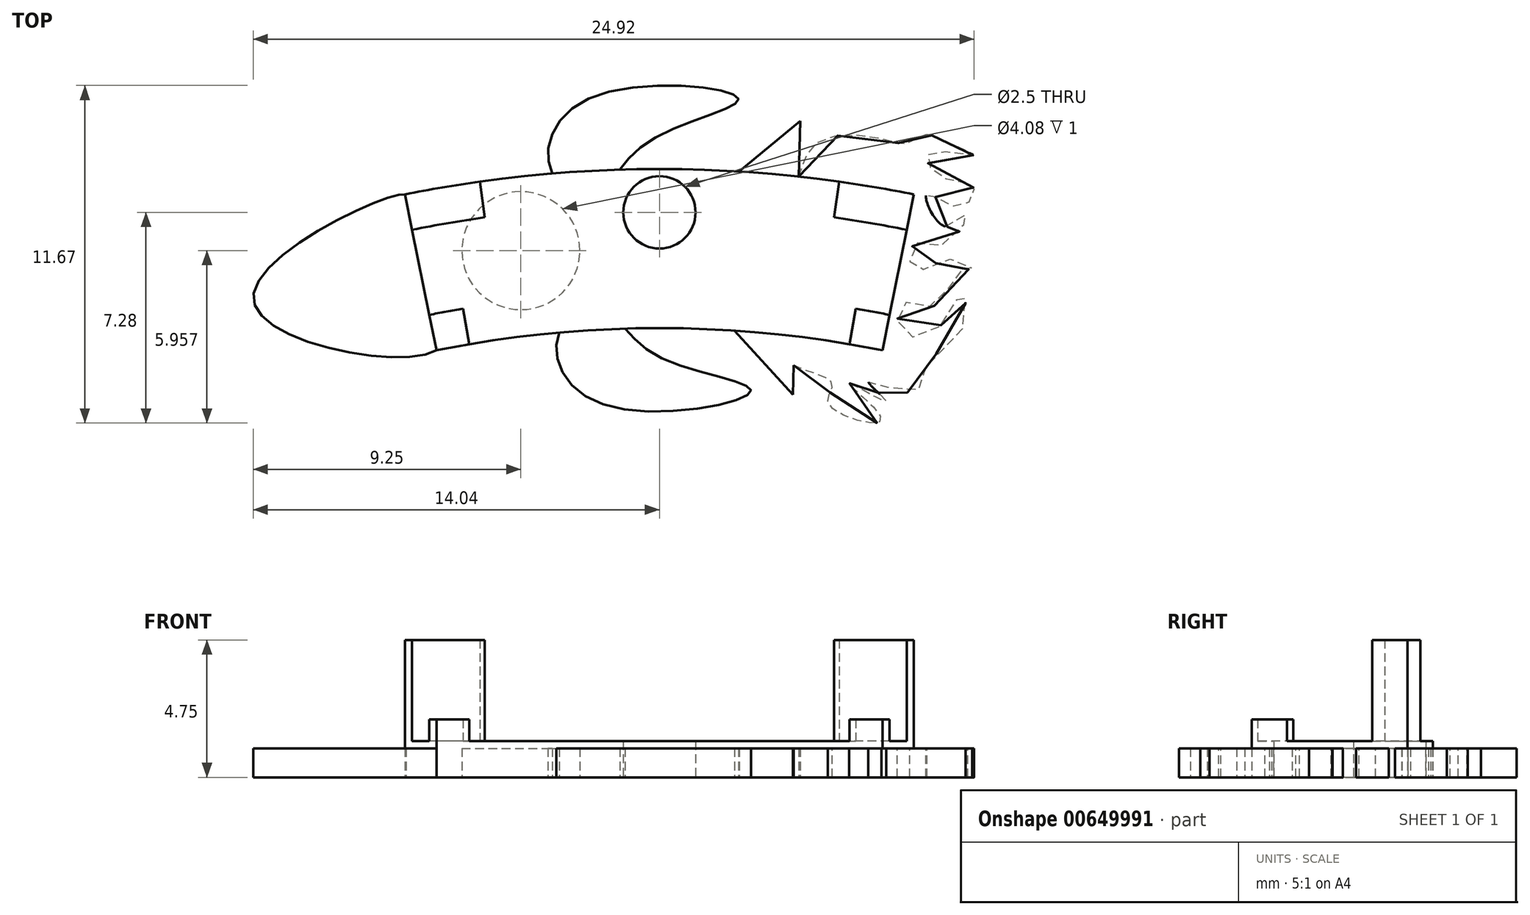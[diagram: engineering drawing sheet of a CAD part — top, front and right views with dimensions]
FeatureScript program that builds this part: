
annotation { "Feature Type Name" : "Feature", "Feature Type Description" : "" }
export const myFeature = defineFeature(function(context is Context, id is Id, definition is map)
    precondition{}
    {
        {
            var Q0;
            Q0=qCreatedBy(makeId("Top.planeOp"),FACE);
            var sketch = newSketch(context, id + "F0", { "sketchPlane" : qUnion([Q0])});
            skCircle(sketch, "E0", {"center": v(0, 0) * mm, "radius": 39 * mm});
            skCircle(sketch, "E1", {"center": v(0, 0) * mm, "radius": 44.5 * mm});
            skCircle(sketch, "E2", {"center": v(0, 43) * mm, "radius": 1.25 * mm});
            skCircle(sketch, "E3", {"center": v(0, 43) * mm, "radius": 6 * mm});
            skLineSegment(sketch, "E4", {"start": v(-7.7, 38.23) * mm, "end": v(-8.8, 43.62) * mm});
            skLineSegment(sketch, "E5", {"start": v(7.7, 38.23) * mm, "end": v(8.8, 43.62) * mm});
            skLineSegment(sketch, "E6", {"start": v(-7.5, 43.86) * mm, "end": v(-6.58, 38.44) * mm});
            skLineSegment(sketch, "E7", {"start": v(6.58, 38.44) * mm, "end": v(7.5, 43.86) * mm});
            skCircle(sketch, "E8", {"center": v(0, 0) * mm, "radius": 40.25 * mm});
            skCircle(sketch, "E9", {"center": v(0, 0) * mm, "radius": 43.25 * mm});
            skSolve(sketch);
        }
        {
            var Q0;
            {var subQ0=sQuery(id+"F0.wireOp",EDGE,"E7");var subQ1=sQuery(id+"F0.wireOp",EDGE,"E1");var subQ2=makeQuery(id+"F0.imprint","INTERSECT",VERTEX,{"derivedFrom":[subQ1,subQ0]});Q0=makeQuery(id+"F0.imprint","IMPRINT",FACE,{"disambiguationData":[TD([[makeQuery(id+"F0.imprint","IMPRINT",EDGE,{"disambiguationData":[TD([[subQ2,-1.0]])],"derivedFrom":subQ1}),1.0]])]});}
            var Q1;
            {var subQ0=sQuery(id+"F0.wireOp",EDGE,"E6");var subQ1=sQuery(id+"F0.wireOp",EDGE,"E1");var subQ2=makeQuery(id+"F0.imprint","INTERSECT",VERTEX,{"derivedFrom":[subQ1,subQ0]});Q1=makeQuery(id+"F0.imprint","IMPRINT",FACE,{"disambiguationData":[TD([[makeQuery(id+"F0.imprint","IMPRINT",EDGE,{"disambiguationData":[TD([[subQ2,1.0]])],"derivedFrom":subQ1}),1.0]])]});}
            var Q2;
            {var subQ0=sQuery(id+"F0.wireOp",EDGE,"E3");var subQ1=sQuery(id+"F0.wireOp",EDGE,"E1");var subQ2=makeQuery(id+"F0.imprint","INTERSECT",VERTEX,{"disambiguationData":[OD(0.0)],"derivedFrom":[subQ1,subQ0]});Q2=makeQuery(id+"F0.imprint","IMPRINT",FACE,{"disambiguationData":[TD([[makeQuery(id+"F0.imprint","IMPRINT",EDGE,{"disambiguationData":[TD([[subQ2,-1.0]])],"derivedFrom":subQ1}),1.0]])]});}
            var Q3;
            {var subQ0=sQuery(id+"F0.wireOp",EDGE,"E8");var subQ1=sQuery(id+"F0.wireOp",EDGE,"E3");var subQ2=makeQuery(id+"F0.imprint","INTERSECT",VERTEX,{"disambiguationData":[OD(1.0)],"derivedFrom":[subQ1,subQ0]});Q3=makeQuery(id+"F0.imprint","IMPRINT",FACE,{"disambiguationData":[TD([[makeQuery(id+"F0.imprint","IMPRINT",EDGE,{"disambiguationData":[TD([[subQ2,-1.0]])],"derivedFrom":subQ1}),-1.0]])]});}
            var Q4;
            {var subQ3=sQuery(id+"F0.wireOp",EDGE,"E9");var subQ5=sQuery(id+"F0.wireOp",EDGE,"E2");var subQ6=makeQuery(id+"F0.imprint","INTERSECT",VERTEX,{"disambiguationData":[OD(0.0)],"derivedFrom":[subQ5,subQ3]});Q4=makeQuery(id+"F0.imprint","IMPRINT",FACE,{"disambiguationData":[TD([[makeQuery(id+"F0.imprint","IMPRINT",EDGE,{"disambiguationData":[TD([[subQ6,1.0]])],"derivedFrom":subQ5}),-1.0]])]});}
            var Q5;
            {var subQ0=sQuery(id+"F0.wireOp",EDGE,"E9");var subQ1=sQuery(id+"F0.wireOp",EDGE,"E3");var subQ2=makeQuery(id+"F0.imprint","INTERSECT",VERTEX,{"disambiguationData":[OD(0.0)],"derivedFrom":[subQ1,subQ0]});Q5=makeQuery(id+"F0.imprint","IMPRINT",FACE,{"disambiguationData":[TD([[makeQuery(id+"F0.imprint","IMPRINT",EDGE,{"disambiguationData":[TD([[subQ2,-1.0]])],"derivedFrom":subQ1}),-1.0]])]});}
            var Q6;
            {var subQ0=sQuery(id+"F0.wireOp",EDGE,"E6");var subQ1=sQuery(id+"F0.wireOp",EDGE,"E0");var subQ2=makeQuery(id+"F0.imprint","INTERSECT",VERTEX,{"derivedFrom":[subQ1,subQ0]});Q6=makeQuery(id+"F0.imprint","IMPRINT",FACE,{"disambiguationData":[TD([[makeQuery(id+"F0.imprint","IMPRINT",EDGE,{"disambiguationData":[TD([[subQ2,1.0]])],"derivedFrom":subQ1}),-1.0]])]});}
            var Q7;
            {var subQ0=sQuery(id+"F0.wireOp",EDGE,"E3");var subQ1=sQuery(id+"F0.wireOp",EDGE,"E0");var subQ2=makeQuery(id+"F0.imprint","INTERSECT",VERTEX,{"disambiguationData":[OD(0.0)],"derivedFrom":[subQ1,subQ0]});Q7=makeQuery(id+"F0.imprint","IMPRINT",FACE,{"disambiguationData":[TD([[makeQuery(id+"F0.imprint","IMPRINT",EDGE,{"disambiguationData":[TD([[subQ2,-1.0]])],"derivedFrom":subQ1}),-1.0]])]});}
            var Q8;
            {var subQ0=sQuery(id+"F0.wireOp",EDGE,"E7");var subQ1=sQuery(id+"F0.wireOp",EDGE,"E0");var subQ2=makeQuery(id+"F0.imprint","INTERSECT",VERTEX,{"derivedFrom":[subQ1,subQ0]});Q8=makeQuery(id+"F0.imprint","IMPRINT",FACE,{"disambiguationData":[TD([[makeQuery(id+"F0.imprint","IMPRINT",EDGE,{"disambiguationData":[TD([[subQ2,-1.0]])],"derivedFrom":subQ1}),-1.0]])]});}
            var Q9;
            {var subQ0=sQuery(id+"F0.wireOp",EDGE,"E8");var subQ1=sQuery(id+"F0.wireOp",EDGE,"E5");var subQ2=makeQuery(id+"F0.imprint","INTERSECT",VERTEX,{"derivedFrom":[subQ1,subQ0]});Q9=makeQuery(id+"F0.imprint","IMPRINT",FACE,{"disambiguationData":[TD([[makeQuery(id+"F0.imprint","IMPRINT",EDGE,{"disambiguationData":[TD([[subQ2,-1.0]])],"derivedFrom":subQ1}),1.0]])]});}
            var Q10;
            {var subQ0=sQuery(id+"F0.wireOp",EDGE,"E8");var subQ1=sQuery(id+"F0.wireOp",EDGE,"E4");var subQ2=makeQuery(id+"F0.imprint","INTERSECT",VERTEX,{"derivedFrom":[subQ1,subQ0]});Q10=makeQuery(id+"F0.imprint","IMPRINT",FACE,{"disambiguationData":[TD([[makeQuery(id+"F0.imprint","IMPRINT",EDGE,{"disambiguationData":[TD([[subQ2,-1.0]])],"derivedFrom":subQ1}),-1.0]])]});}
            extrude(context, id + "F1", {"entities" : qUnion([Q0, Q1, Q2, Q3, Q4, Q5, Q6, Q7, Q8, Q9, Q10]), "depth" : 1.25 * mm, "offsetDistance" : 25 * mm});
        }
        {
            var Q0;
            Q0=qCreatedBy(makeId("Top.planeOp"),FACE);
            var sketch = newSketch(context, id + "F2", { "sketchPlane" : qUnion([Q0])});
            skCircle(sketch, "E10", {"center": v(0, 0) * mm, "radius": 39 * mm});
            skCircle(sketch, "E11", {"center": v(0, 0) * mm, "radius": 44.5 * mm});
            skCircle(sketch, "E12", {"center": v(0, 43) * mm, "radius": 0.85 * mm});
            skCircle(sketch, "E13", {"center": v(0, 43) * mm, "radius": 6 * mm});
            skLineSegment(sketch, "E14", {"start": v(-7.7, 38.23) * mm, "end": v(-8.8, 43.62) * mm});
            skLineSegment(sketch, "E15", {"start": v(7.7, 38.23) * mm, "end": v(8.8, 43.62) * mm});
            skLineSegment(sketch, "E16", {"start": v(-6.2, 44.06) * mm, "end": v(-5.44, 38.62) * mm});
            skLineSegment(sketch, "E17", {"start": v(5.44, 38.62) * mm, "end": v(6.2, 44.06) * mm});
            skCircle(sketch, "E18", {"center": v(0, 0) * mm, "radius": 40.25 * mm});
            skCircle(sketch, "E19", {"center": v(0, 0) * mm, "radius": 43.25 * mm});
            skSolve(sketch);
        }
        {
            var Q0;
            {var subQ0=sQuery(id+"F2.wireOp",EDGE,"E15");var subQ1=sQuery(id+"F2.wireOp",EDGE,"E11");var subQ2=makeQuery(id+"F2.imprint","INTERSECT",VERTEX,{"derivedFrom":[subQ1,subQ0]});Q0=makeQuery(id+"F2.imprint","IMPRINT",FACE,{"disambiguationData":[TD([[makeQuery(id+"F2.imprint","IMPRINT",EDGE,{"disambiguationData":[TD([[subQ2,-1.0]])],"derivedFrom":subQ1}),1.0]])]});}
            var Q1;
            {var subQ0=sQuery(id+"F2.wireOp",EDGE,"E14");var subQ1=sQuery(id+"F2.wireOp",EDGE,"E11");var subQ2=makeQuery(id+"F2.imprint","INTERSECT",VERTEX,{"derivedFrom":[subQ1,subQ0]});Q1=makeQuery(id+"F2.imprint","IMPRINT",FACE,{"disambiguationData":[TD([[makeQuery(id+"F2.imprint","IMPRINT",EDGE,{"disambiguationData":[TD([[subQ2,1.0]])],"derivedFrom":subQ1}),1.0]])]});}
            extrude(context, id + "F3", {"entities" : qUnion([Q0, Q1]), "operationType" : NewBodyOperationType.ADD, "depth" : 4.75 * mm, "offsetDistance" : 25 * mm});
        }
        {
            var Q0;
            Q0=qCreatedBy(makeId("Top.planeOp"),FACE);
            var sketch = newSketch(context, id + "F4", { "sketchPlane" : qUnion([Q0])});
            skCircle(sketch, "E20", {"center": v(0, 0) * mm, "radius": 39 * mm});
            skCircle(sketch, "E21", {"center": v(0, 0) * mm, "radius": 44.5 * mm});
            skCircle(sketch, "E22", {"center": v(0, 43) * mm, "radius": 0.85 * mm});
            skCircle(sketch, "E23", {"center": v(0, 43) * mm, "radius": 6 * mm});
            skLineSegment(sketch, "E24", {"start": v(-7.7, 38.23) * mm, "end": v(-8.8, 43.62) * mm});
            skLineSegment(sketch, "E25", {"start": v(7.7, 38.23) * mm, "end": v(8.8, 43.62) * mm});
            skLineSegment(sketch, "E26", {"start": v(-7.5, 43.86) * mm, "end": v(-6.58, 38.44) * mm});
            skLineSegment(sketch, "E27", {"start": v(6.58, 38.44) * mm, "end": v(7.5, 43.86) * mm});
            skCircle(sketch, "E28", {"center": v(0, 0) * mm, "radius": 40.25 * mm});
            skCircle(sketch, "E29", {"center": v(0, 0) * mm, "radius": 43.25 * mm});
            skSolve(sketch);
        }
        {
            var Q0;
            {var subQ0=sQuery(id+"F4.wireOp",EDGE,"E24");var subQ1=sQuery(id+"F4.wireOp",EDGE,"E20");var subQ2=makeQuery(id+"F4.imprint","INTERSECT",VERTEX,{"derivedFrom":[subQ1,subQ0]});Q0=makeQuery(id+"F4.imprint","IMPRINT",FACE,{"disambiguationData":[TD([[makeQuery(id+"F4.imprint","IMPRINT",EDGE,{"disambiguationData":[TD([[subQ2,1.0]])],"derivedFrom":subQ1}),-1.0]])]});}
            var Q1;
            {var subQ0=sQuery(id+"F4.wireOp",EDGE,"E25");var subQ1=sQuery(id+"F4.wireOp",EDGE,"E20");var subQ2=makeQuery(id+"F4.imprint","INTERSECT",VERTEX,{"derivedFrom":[subQ1,subQ0]});Q1=makeQuery(id+"F4.imprint","IMPRINT",FACE,{"disambiguationData":[TD([[makeQuery(id+"F4.imprint","IMPRINT",EDGE,{"disambiguationData":[TD([[subQ2,-1.0]])],"derivedFrom":subQ1}),-1.0]])]});}
            extrude(context, id + "F5", {"entities" : qUnion([Q0, Q1]), "operationType" : NewBodyOperationType.ADD, "depth" : 2 * mm, "offsetDistance" : 25 * mm});
        }
        {
            var Q0;
            {var subQ0=sQuery(id+"F4.wireOp",EDGE,"E28");var subQ1=sQuery(id+"F4.wireOp",EDGE,"E20");var subQ2=sQuery(id+"F2.wireOp",EDGE,"E19");var subQ3=sQuery(id+"F2.wireOp",EDGE,"E11");Q0=makeQuery(id+"F5.boolean.opBoolean","MERGE",FACE,{"derivedFrom":[makeQuery(id+"F3.boolean.opBoolean","MERGE",FACE,{"derivedFrom":[makeQuery(id+"F1.opExtrude","CAP_FACE",FACE,{"disambiguationData":[OSD([sQuery(id+"F0.wireOp",EDGE,"E0"),sQuery(id+"F0.wireOp",EDGE,"E1"),sQuery(id+"F0.wireOp",EDGE,"E2"),sQuery(id+"F0.wireOp",EDGE,"E4"),sQuery(id+"F0.wireOp",EDGE,"E5"),sQuery(id+"F0.wireOp",EDGE,"E6"),sQuery(id+"F0.wireOp",EDGE,"E7"),sQuery(id+"F0.wireOp",EDGE,"E8"),sQuery(id+"F0.wireOp",EDGE,"E9")])],"isStart":true}),makeQuery(id+"F3.opExtrude","CAP_FACE",FACE,{"disambiguationData":[OSD([subQ3,sQuery(id+"F2.wireOp",EDGE,"E15"),sQuery(id+"F2.wireOp",EDGE,"E17"),subQ2])],"isStart":true}),makeQuery(id+"F3.opExtrude","CAP_FACE",FACE,{"disambiguationData":[OSD([subQ3,sQuery(id+"F2.wireOp",EDGE,"E14"),sQuery(id+"F2.wireOp",EDGE,"E16"),subQ2])],"isStart":true})]}),makeQuery(id+"F5.opExtrude","CAP_FACE",FACE,{"disambiguationData":[OSD([subQ1,sQuery(id+"F4.wireOp",EDGE,"E25"),sQuery(id+"F4.wireOp",EDGE,"E27"),subQ0])],"isStart":true}),makeQuery(id+"F5.opExtrude","CAP_FACE",FACE,{"disambiguationData":[OSD([subQ1,sQuery(id+"F4.wireOp",EDGE,"E24"),sQuery(id+"F4.wireOp",EDGE,"E26"),subQ0])],"isStart":true})]});}
            var sketch = newSketch(context, id + "F6", { "sketchPlane" : qUnion([Q0])});
            skFitSpline(sketch, "E30", {"points": [v(-8.8, -43.62) * mm, v(-14.04, -40.05) * mm, v(-7.7, -38.23) * mm, v(-7.7, -39.96) * mm, v(-8, -41.27) * mm, v(-8.21, -42.6) * mm, v(-8.43, -43.18) * mm, v(-8.75, -43.41) * mm, v(-8.8, -43.62) * mm]});
            skSolve(sketch);
        }
        {
            var Q0;
            Q0 = qSketchRegion(id + "F6", true);
            extrude(context, id + "F7", {"entities" : qUnion([Q0]), "operationType" : NewBodyOperationType.ADD, "oppositeDirection" : true, "depth" : 1 * mm, "offsetDistance" : 25 * mm});
        }
        {
            var Q0;
            {var subQ0=sQuery(id+"F4.wireOp",EDGE,"E28");var subQ1=sQuery(id+"F4.wireOp",EDGE,"E20");var subQ2=sQuery(id+"F2.wireOp",EDGE,"E19");var subQ3=sQuery(id+"F2.wireOp",EDGE,"E11");Q0=makeQuery(id+"F7.boolean.opBoolean","MERGE",FACE,{"derivedFrom":[makeQuery(id+"F5.boolean.opBoolean","MERGE",FACE,{"derivedFrom":[makeQuery(id+"F3.boolean.opBoolean","MERGE",FACE,{"derivedFrom":[makeQuery(id+"F1.opExtrude","CAP_FACE",FACE,{"disambiguationData":[OSD([sQuery(id+"F0.wireOp",EDGE,"E0"),sQuery(id+"F0.wireOp",EDGE,"E1"),sQuery(id+"F0.wireOp",EDGE,"E2"),sQuery(id+"F0.wireOp",EDGE,"E4"),sQuery(id+"F0.wireOp",EDGE,"E5"),sQuery(id+"F0.wireOp",EDGE,"E6"),sQuery(id+"F0.wireOp",EDGE,"E7"),sQuery(id+"F0.wireOp",EDGE,"E8"),sQuery(id+"F0.wireOp",EDGE,"E9")])],"isStart":true}),makeQuery(id+"F3.opExtrude","CAP_FACE",FACE,{"disambiguationData":[OSD([subQ3,sQuery(id+"F2.wireOp",EDGE,"E15"),sQuery(id+"F2.wireOp",EDGE,"E17"),subQ2])],"isStart":true}),makeQuery(id+"F3.opExtrude","CAP_FACE",FACE,{"disambiguationData":[OSD([subQ3,sQuery(id+"F2.wireOp",EDGE,"E14"),sQuery(id+"F2.wireOp",EDGE,"E16"),subQ2])],"isStart":true})]}),makeQuery(id+"F5.opExtrude","CAP_FACE",FACE,{"disambiguationData":[OSD([subQ1,sQuery(id+"F4.wireOp",EDGE,"E25"),sQuery(id+"F4.wireOp",EDGE,"E27"),subQ0])],"isStart":true}),makeQuery(id+"F5.opExtrude","CAP_FACE",FACE,{"disambiguationData":[OSD([subQ1,sQuery(id+"F4.wireOp",EDGE,"E24"),sQuery(id+"F4.wireOp",EDGE,"E26"),subQ0])],"isStart":true})]}),makeQuery(id+"F7.opExtrude","CAP_FACE",FACE,{"disambiguationData":[OSD([sQuery(id+"F6.wireOp",EDGE,"E30")])],"isStart":true})]});}
            var sketch = newSketch(context, id + "F8", { "sketchPlane" : qUnion([Q0])});
            skCircle(sketch, "E31", {"center": v(-4.8, -41.68) * mm, "radius": 2.04 * mm});
            skSolve(sketch);
        }
        {
            var Q0;
            Q0 = qSketchRegion(id + "F8", true);
            extrude(context, id + "F9", {"entities" : qUnion([Q0]), "operationType" : NewBodyOperationType.REMOVE, "oppositeDirection" : true, "depth" : 1 * mm, "offsetDistance" : 25 * mm});
        }
        {
            var Q0;
            {var subQ0=sQuery(id+"F4.wireOp",EDGE,"E28");var subQ1=sQuery(id+"F4.wireOp",EDGE,"E20");var subQ2=sQuery(id+"F2.wireOp",EDGE,"E19");var subQ3=sQuery(id+"F2.wireOp",EDGE,"E11");Q0=makeQuery(id+"F7.boolean.opBoolean","MERGE",FACE,{"derivedFrom":[makeQuery(id+"F5.boolean.opBoolean","MERGE",FACE,{"derivedFrom":[makeQuery(id+"F3.boolean.opBoolean","MERGE",FACE,{"derivedFrom":[makeQuery(id+"F1.opExtrude","CAP_FACE",FACE,{"disambiguationData":[OSD([sQuery(id+"F0.wireOp",EDGE,"E0"),sQuery(id+"F0.wireOp",EDGE,"E1"),sQuery(id+"F0.wireOp",EDGE,"E2"),sQuery(id+"F0.wireOp",EDGE,"E4"),sQuery(id+"F0.wireOp",EDGE,"E5"),sQuery(id+"F0.wireOp",EDGE,"E6"),sQuery(id+"F0.wireOp",EDGE,"E7"),sQuery(id+"F0.wireOp",EDGE,"E8"),sQuery(id+"F0.wireOp",EDGE,"E9")])],"isStart":true}),makeQuery(id+"F3.opExtrude","CAP_FACE",FACE,{"disambiguationData":[OSD([subQ3,sQuery(id+"F2.wireOp",EDGE,"E15"),sQuery(id+"F2.wireOp",EDGE,"E17"),subQ2])],"isStart":true}),makeQuery(id+"F3.opExtrude","CAP_FACE",FACE,{"disambiguationData":[OSD([subQ3,sQuery(id+"F2.wireOp",EDGE,"E14"),sQuery(id+"F2.wireOp",EDGE,"E16"),subQ2])],"isStart":true})]}),makeQuery(id+"F5.opExtrude","CAP_FACE",FACE,{"disambiguationData":[OSD([subQ1,sQuery(id+"F4.wireOp",EDGE,"E25"),sQuery(id+"F4.wireOp",EDGE,"E27"),subQ0])],"isStart":true}),makeQuery(id+"F5.opExtrude","CAP_FACE",FACE,{"disambiguationData":[OSD([subQ1,sQuery(id+"F4.wireOp",EDGE,"E24"),sQuery(id+"F4.wireOp",EDGE,"E26"),subQ0])],"isStart":true})]}),makeQuery(id+"F7.opExtrude","CAP_FACE",FACE,{"disambiguationData":[OSD([sQuery(id+"F6.wireOp",EDGE,"E30")])],"isStart":true})]});}
            var sketch = newSketch(context, id + "F10", { "sketchPlane" : qUnion([Q0])});
            skFitSpline(sketch, "E32", {"points": [v(-2.2, -43.63) * mm, v(-3.7, -44.35) * mm, v(-2.48, -46.91) * mm, v(2.73, -46.92) * mm, v(-0.49, -45.38) * mm, v(-2.2, -43.63) * mm]});
            skLineSegment(sketch, "E33", {"start": v(3.58, -41.9) * mm, "end": v(-9.05, -41.36) * mm});
            skFitSpline(sketch, "E34.MirrorC", {"points": [v(-2.03, -39.69) * mm, v(-3.46, -38.84) * mm, v(-2.03, -36.4) * mm, v(3.16, -36.83) * mm, v(-0.17, -38.1) * mm, v(-2.03, -39.69) * mm]});
            skSolve(sketch);
        }
        {
            var Q0;
            Q0 = qSketchRegion(id + "F10", true);
            extrude(context, id + "F11", {"entities" : qUnion([Q0]), "operationType" : NewBodyOperationType.ADD, "oppositeDirection" : true, "depth" : 1 * mm, "offsetDistance" : 25 * mm});
        }
        {
            var Q0;
            {var subQ0=sQuery(id+"F4.wireOp",EDGE,"E28");var subQ1=sQuery(id+"F4.wireOp",EDGE,"E20");var subQ2=sQuery(id+"F2.wireOp",EDGE,"E19");var subQ3=sQuery(id+"F2.wireOp",EDGE,"E11");Q0=makeQuery(id+"F11.boolean.opBoolean","MERGE",FACE,{"derivedFrom":[makeQuery(id+"F7.boolean.opBoolean","MERGE",FACE,{"derivedFrom":[makeQuery(id+"F5.boolean.opBoolean","MERGE",FACE,{"derivedFrom":[makeQuery(id+"F3.boolean.opBoolean","MERGE",FACE,{"derivedFrom":[makeQuery(id+"F1.opExtrude","CAP_FACE",FACE,{"disambiguationData":[OSD([sQuery(id+"F0.wireOp",EDGE,"E0"),sQuery(id+"F0.wireOp",EDGE,"E1"),sQuery(id+"F0.wireOp",EDGE,"E2"),sQuery(id+"F0.wireOp",EDGE,"E4"),sQuery(id+"F0.wireOp",EDGE,"E5"),sQuery(id+"F0.wireOp",EDGE,"E6"),sQuery(id+"F0.wireOp",EDGE,"E7"),sQuery(id+"F0.wireOp",EDGE,"E8"),sQuery(id+"F0.wireOp",EDGE,"E9")])],"isStart":true}),makeQuery(id+"F3.opExtrude","CAP_FACE",FACE,{"disambiguationData":[OSD([subQ3,sQuery(id+"F2.wireOp",EDGE,"E15"),sQuery(id+"F2.wireOp",EDGE,"E17"),subQ2])],"isStart":true}),makeQuery(id+"F3.opExtrude","CAP_FACE",FACE,{"disambiguationData":[OSD([subQ3,sQuery(id+"F2.wireOp",EDGE,"E14"),sQuery(id+"F2.wireOp",EDGE,"E16"),subQ2])],"isStart":true})]}),makeQuery(id+"F5.opExtrude","CAP_FACE",FACE,{"disambiguationData":[OSD([subQ1,sQuery(id+"F4.wireOp",EDGE,"E25"),sQuery(id+"F4.wireOp",EDGE,"E27"),subQ0])],"isStart":true}),makeQuery(id+"F5.opExtrude","CAP_FACE",FACE,{"disambiguationData":[OSD([subQ1,sQuery(id+"F4.wireOp",EDGE,"E24"),sQuery(id+"F4.wireOp",EDGE,"E26"),subQ0])],"isStart":true})]}),makeQuery(id+"F7.opExtrude","CAP_FACE",FACE,{"disambiguationData":[OSD([sQuery(id+"F6.wireOp",EDGE,"E30")])],"isStart":true})]}),makeQuery(id+"F11.opExtrude","CAP_FACE",FACE,{"disambiguationData":[OSD([sQuery(id+"F10.wireOp",EDGE,"E32")])],"isStart":true}),makeQuery(id+"F11.opExtrude","CAP_FACE",FACE,{"disambiguationData":[OSD([sQuery(id+"F10.wireOp",EDGE,"E34.MirrorC")])],"isStart":true})]});}
            var sketch = newSketch(context, id + "F12", { "sketchPlane" : qUnion([Q0])});
            skLineSegment(sketch, "E35", {"start": v(2.76, -44.41) * mm, "end": v(4.86, -46.16) * mm});
            skLineSegment(sketch, "E36", {"start": v(4.86, -46.16) * mm, "end": v(4.62, -36.7) * mm});
            skLineSegment(sketch, "E37", {"start": v(4.62, -36.7) * mm, "end": v(2.6, -38.91) * mm});
            skLineSegment(sketch, "E38", {"start": v(2.6, -38.91) * mm, "end": v(2.76, -44.41) * mm});
            skSolve(sketch);
        }
        {
            var Q0;
            Q0 = qSketchRegion(id + "F12", true);
            extrude(context, id + "F13", {"entities" : qUnion([Q0]), "operationType" : NewBodyOperationType.ADD, "oppositeDirection" : true, "depth" : 1 * mm, "offsetDistance" : 25 * mm});
        }
        {
            var Q0;
            {var subQ0=sQuery(id+"F4.wireOp",EDGE,"E28");var subQ1=sQuery(id+"F4.wireOp",EDGE,"E20");var subQ2=sQuery(id+"F2.wireOp",EDGE,"E19");var subQ3=sQuery(id+"F2.wireOp",EDGE,"E11");Q0=makeQuery(id+"F13.boolean.opBoolean","MERGE",FACE,{"derivedFrom":[makeQuery(id+"F11.boolean.opBoolean","MERGE",FACE,{"derivedFrom":[makeQuery(id+"F7.boolean.opBoolean","MERGE",FACE,{"derivedFrom":[makeQuery(id+"F5.boolean.opBoolean","MERGE",FACE,{"derivedFrom":[makeQuery(id+"F3.boolean.opBoolean","MERGE",FACE,{"derivedFrom":[makeQuery(id+"F1.opExtrude","CAP_FACE",FACE,{"disambiguationData":[OSD([sQuery(id+"F0.wireOp",EDGE,"E0"),sQuery(id+"F0.wireOp",EDGE,"E1"),sQuery(id+"F0.wireOp",EDGE,"E2"),sQuery(id+"F0.wireOp",EDGE,"E4"),sQuery(id+"F0.wireOp",EDGE,"E5"),sQuery(id+"F0.wireOp",EDGE,"E6"),sQuery(id+"F0.wireOp",EDGE,"E7"),sQuery(id+"F0.wireOp",EDGE,"E8"),sQuery(id+"F0.wireOp",EDGE,"E9")])],"isStart":true}),makeQuery(id+"F3.opExtrude","CAP_FACE",FACE,{"disambiguationData":[OSD([subQ3,sQuery(id+"F2.wireOp",EDGE,"E15"),sQuery(id+"F2.wireOp",EDGE,"E17"),subQ2])],"isStart":true}),makeQuery(id+"F3.opExtrude","CAP_FACE",FACE,{"disambiguationData":[OSD([subQ3,sQuery(id+"F2.wireOp",EDGE,"E14"),sQuery(id+"F2.wireOp",EDGE,"E16"),subQ2])],"isStart":true})]}),makeQuery(id+"F5.opExtrude","CAP_FACE",FACE,{"disambiguationData":[OSD([subQ1,sQuery(id+"F4.wireOp",EDGE,"E25"),sQuery(id+"F4.wireOp",EDGE,"E27"),subQ0])],"isStart":true}),makeQuery(id+"F5.opExtrude","CAP_FACE",FACE,{"disambiguationData":[OSD([subQ1,sQuery(id+"F4.wireOp",EDGE,"E24"),sQuery(id+"F4.wireOp",EDGE,"E26"),subQ0])],"isStart":true})]}),makeQuery(id+"F7.opExtrude","CAP_FACE",FACE,{"disambiguationData":[OSD([sQuery(id+"F6.wireOp",EDGE,"E30")])],"isStart":true})]}),makeQuery(id+"F11.opExtrude","CAP_FACE",FACE,{"disambiguationData":[OSD([sQuery(id+"F10.wireOp",EDGE,"E32")])],"isStart":true}),makeQuery(id+"F11.opExtrude","CAP_FACE",FACE,{"disambiguationData":[OSD([sQuery(id+"F10.wireOp",EDGE,"E34.MirrorC")])],"isStart":true})]}),makeQuery(id+"F13.opExtrude","CAP_FACE",FACE,{"disambiguationData":[OSD([sQuery(id+"F12.wireOp",EDGE,"E35"),sQuery(id+"F12.wireOp",EDGE,"E36"),sQuery(id+"F12.wireOp",EDGE,"E37"),sQuery(id+"F12.wireOp",EDGE,"E38")])],"isStart":true})]});}
            var sketch = newSketch(context, id + "F14", { "sketchPlane" : qUnion([Q0])});
            skFitSpline(sketch, "E39", {"points": [v(4.81, -44.24) * mm, v(5.73, -45.55) * mm, v(7.72, -45.54) * mm, v(8.58, -45.39) * mm, v(9.1, -45.69) * mm, v(9.96, -45.42) * mm, v(10.87, -44.98) * mm, v(9.33, -45.02) * mm, v(9.74, -44.24) * mm, v(10.86, -43.85) * mm, v(10.36, -43.18) * mm, v(9.24, -43.62) * mm, v(9.92, -42.51) * mm, v(10.66, -42.97) * mm, v(9.9, -41.9) * mm, v(8.8, -41.89) * mm, v(8.8, -41) * mm, v(10.07, -41.39) * mm, v(10.82, -41.02) * mm, v(10.4, -41) * mm, v(9.53, -39.78) * mm, v(8.44, -39.85) * mm, v(8.37, -38.9) * mm, v(9.7, -39.06) * mm, v(10.48, -40.22) * mm, v(10.4, -38.8) * mm, v(9.29, -37.83) * mm, v(8.8, -36.78) * mm, v(7.22, -37.15) * mm, v(7.84, -36.46) * mm, v(6.56, -37.09) * mm, v(7.67, -35.83) * mm, v(5.87, -36.34) * mm, v(5.98, -37.07) * mm, v(4.64, -37.71) * mm, v(4.06, -38.97) * mm, v(4.81, -44.24) * mm]});
            skSolve(sketch);
        }
        {
            var Q0;
            Q0 = qSketchRegion(id + "F14", true);
            extrude(context, id + "F15", {"entities" : qUnion([Q0]), "operationType" : NewBodyOperationType.ADD, "oppositeDirection" : true, "depth" : 1 * mm, "offsetDistance" : 25 * mm});
        }
    });
